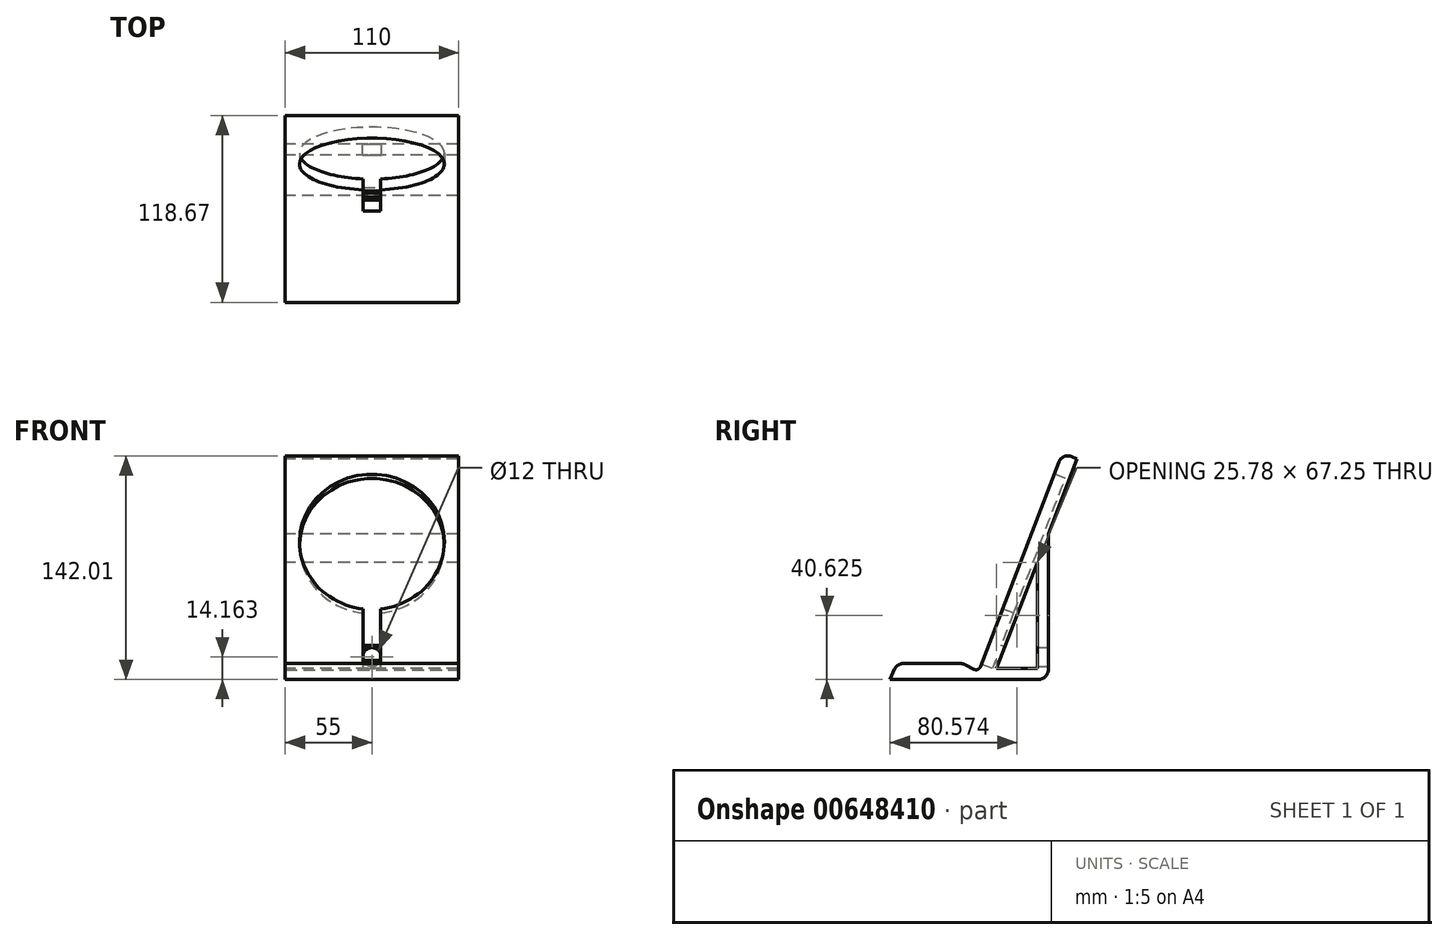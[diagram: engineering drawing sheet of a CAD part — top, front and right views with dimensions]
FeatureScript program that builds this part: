
annotation { "Feature Type Name" : "Feature", "Feature Type Description" : "" }
export const myFeature = defineFeature(function(context is Context, id is Id, definition is map)
    precondition{}
    {
        {
            var Q0;
            Q0=qCreatedBy(makeId("Right.planeOp"),FACE);
            var sketch = newSketch(context, id + "F0", { "sketchPlane" : qUnion([Q0])});
            skLineSegment(sketch, "E0", {"start": v(-0.23, -35.33) * mm, "end": v(53.11, 103.83) * mm});
            skLineSegment(sketch, "E1.0", {"start": v(8.6, -40.22) * mm, "end": v(62.27, 99.78) * mm});
            skLineSegment(sketch, "E1.1", {"start": v(-56.4, -40.11) * mm, "end": v(8.6, -40.22) * mm});
            skLineSegment(sketch, "E2", {"start": v(-51.97, -30.12) * mm, "end": v(-56.4, -40.11) * mm});
            skLineSegment(sketch, "E3", {"start": v(62.27, 99.78) * mm, "end": v(53.11, 103.83) * mm});
            skLineSegment(sketch, "E4", {"start": v(-9.93, -30.2) * mm, "end": v(-0.23, -35.33) * mm});
            skPoint(sketch, "E5.orphan", {"position": v(0, -34.72) * mm});
            skLineSegment(sketch, "E6", {"start": v(-9.93, -30.2) * mm, "end": v(-51.97, -30.12) * mm});
            skLineSegment(sketch, "E7", {"start": v(37.06, 34.03) * mm, "end": v(37.06, -33.22) * mm});
            skLineSegment(sketch, "E8", {"start": v(44.06, -40.22) * mm, "end": v(8.6, -40.22) * mm});
            skLineSegment(sketch, "E9.0", {"start": v(44.06, 52.3) * mm, "end": v(44.06, -40.22) * mm});
            skLineSegment(sketch, "E10.0", {"start": v(37.06, -33.22) * mm, "end": v(11.28, -33.22) * mm});
            skPoint(sketch, "E11.orphan", {"position": v(37.06, -40.22) * mm});
            skSolve(sketch);
        }
        {
            var Q0;
            {var subQ0=sQuery(id+"F0.wireOp",EDGE,"E7");Q0=makeQuery(id+"F0.imprint","IMPRINT",FACE,{"disambiguationData":[TD([[makeQuery(id+"F0.imprint","IMPRINT",EDGE,{"derivedFrom":subQ0}),1.0]])]});}
            var Q1;
            Q1=makeQuery(id+"F0.imprint","IMPRINT",FACE,{"disambiguationData":[TD([[makeQuery(id+"F0.imprint","IMPRINT",EDGE,{"derivedFrom":sQuery(id+"F0.wireOp",EDGE,"E0")}),-1.0]])]});
            extrude(context, id + "F1", {"entities" : qUnion([Q0, Q1]), "endBound" : BoundingType.SYMMETRIC, "depth" : 110 * mm, "offsetDistance" : 25 * mm});
        }
        {
            var Q0;
            Q0=makeQuery(id+"F1.opExtrude","SWEPT_EDGE",EDGE,{"disambiguationData":[OSD([sQuery(id+"F0.wireOp",EDGE,"E4"),sQuery(id+"F0.wireOp",EDGE,"E6")])]});
            var Q1;
            Q1=makeQuery(id+"F1.opExtrude","SWEPT_EDGE",EDGE,{"disambiguationData":[OSD([sQuery(id+"F0.wireOp",EDGE,"E2"),sQuery(id+"F0.wireOp",EDGE,"E6")])]});
            var Q2;
            Q2=makeQuery(id+"F1.opExtrude","SWEPT_EDGE",EDGE,{"disambiguationData":[OSD([sQuery(id+"F0.wireOp",EDGE,"E8"),sQuery(id+"F0.wireOp",EDGE,"E9.0")])]});
            var Q3;
            Q3=makeQuery(id+"F1.opExtrude","SWEPT_EDGE",EDGE,{"disambiguationData":[OSD([sQuery(id+"F0.wireOp",EDGE,"E0"),sQuery(id+"F0.wireOp",EDGE,"E3")])]});
            fillet(context, id + "F2", {"entities" : qUnion([Q0, Q1, Q2, Q3]), "radius" : 6 * mm, "tangentPropagation" : true, "allowEdgeOverflow" : false});
        }
        {
            var Q0;
            Q0=makeQuery(id+"F1.opExtrude","SWEPT_EDGE",EDGE,{"disambiguationData":[OSD([sQuery(id+"F0.wireOp",EDGE,"E0"),sQuery(id+"F0.wireOp",EDGE,"E4")])]});
            fillet(context, id + "F3", {"entities" : qUnion([Q0]), "radius" : 3 * mm, "tangentPropagation" : true, "allowEdgeOverflow" : false});
        }
        {
            var Q0;
            Q0=makeQuery(id+"F1.opExtrude","SWEPT_FACE",FACE,{"disambiguationData":[OSD([sQuery(id+"F0.wireOp",EDGE,"E0")])]});
            var sketch = newSketch(context, id + "F4", { "sketchPlane" : qUnion([Q0])});
            skPoint(sketch, "E12", {"position": v(0, 55.31) * mm});
            skArc(sketch, "E13", {"start": v(5.5, 10.55) * mm, "mid": v(0, 100.41) * mm, "end": v(-5.5, 10.55) * mm});
            skArc(sketch, "E14", {"start": v(5.5, 9.64) * mm, "mid": v(0, 101.31) * mm, "end": v(-5.5, 9.64) * mm});
            skPoint(sketch, "E15.middle", {"position": v(-5.97, 9.58) * mm});
            skLineSegment(sketch, "E16.bottom", {"start": v(-5.5, 10.6) * mm, "end": v(5.5, 10.6) * mm});
            skLineSegment(sketch, "E16.top", {"start": v(-5.5, -28.02) * mm, "end": v(5.5, -28.02) * mm});
            skLineSegment(sketch, "E16.left", {"start": v(-5.5, 10.6) * mm, "end": v(-5.5, 10.55) * mm});
            skLineSegment(sketch, "E16.right", {"start": v(5.5, 10.6) * mm, "end": v(5.5, 10.55) * mm});
            skPoint(sketch, "E16.middle", {"position": v(0, -8.71) * mm});
            skLineSegment(sketch, "E17.trimOffspring", {"start": v(5.5, 9.64) * mm, "end": v(5.5, -28.02) * mm});
            skLineSegment(sketch, "E18.trimOffspring", {"start": v(-5.5, 9.64) * mm, "end": v(-5.5, -28.02) * mm});
            skSolve(sketch);
        }
        {
            var Q0;
            {var subQ5=sQuery(id+"F4.wireOp",EDGE,"E16.bottom");Q0=makeQuery(id+"F4.imprint","IMPRINT",FACE,{"disambiguationData":[TD([[makeQuery(id+"F4.imprint","IMPRINT",EDGE,{"derivedFrom":subQ5}),1.0]])]});}
            var Q1;
            {var subQ5=sQuery(id+"F4.wireOp",EDGE,"E16.top");Q1=makeQuery(id+"F4.imprint","IMPRINT",FACE,{"disambiguationData":[TD([[makeQuery(id+"F4.imprint","IMPRINT",EDGE,{"derivedFrom":subQ5}),1.0]])]});}
            var Q2;
            {var subQ0=sQuery(id+"F4.wireOp",EDGE,"E16.left");var subQ1=sQuery(id+"F4.wireOp",EDGE,"E13");var subQ2=makeQuery(id+"F4.imprint","INTERSECT",VERTEX,{"derivedFrom":[subQ1,subQ0]});Q2=makeQuery(id+"F4.imprint","IMPRINT",FACE,{"disambiguationData":[TD([[makeQuery(id+"F4.imprint","IMPRINT",EDGE,{"disambiguationData":[TD([[subQ2,-1.0]])],"derivedFrom":subQ1}),-1.0]])]});}
            extrude(context, id + "F5", {"entities" : qUnion([Q0, Q1, Q2]), "operationType" : NewBodyOperationType.REMOVE, "oppositeDirection" : true, "depth" : 7.5 * mm, "offsetDistance" : 25 * mm});
        }
        {
            var Q0;
            Q0=makeQuery(id+"F5.boolean.opBoolean","COPY",FACE,{"derivedFrom":makeQuery(id+"F5.opExtrude","CAP_FACE",FACE,{"disambiguationData":[OSD([sQuery(id+"F4.wireOp",EDGE,"E14"),sQuery(id+"F4.wireOp",EDGE,"E16.top"),sQuery(id+"F4.wireOp",EDGE,"E17.trimOffspring"),sQuery(id+"F4.wireOp",EDGE,"E18.trimOffspring")])],"isStart":false})});
            var sketch = newSketch(context, id + "F6", { "sketchPlane" : qUnion([Q0])});
            skLineSegment(sketch, "E19.bottom", {"start": v(-5.5, -22.47) * mm, "end": v(5.5, -22.47) * mm});
            skLineSegment(sketch, "E19.top", {"start": v(-5.5, -12.47) * mm, "end": v(5.5, -12.47) * mm});
            skLineSegment(sketch, "E19.left", {"start": v(-5.5, -22.47) * mm, "end": v(-5.5, -12.47) * mm});
            skLineSegment(sketch, "E19.right", {"start": v(5.5, -22.47) * mm, "end": v(5.5, -12.47) * mm});
            skPoint(sketch, "E19.middle", {"position": v(0, -17.47) * mm});
            skSolve(sketch);
        }
        {
            var Q0;
            Q0 = qSketchRegion(id + "F6", true);
            extrude(context, id + "F7", {"entities" : qUnion([Q0]), "operationType" : NewBodyOperationType.REMOVE, "oppositeDirection" : true, "depth" : 12 * mm, "offsetDistance" : 25 * mm});
        }
        {
            var Q0;
            Q0=makeQuery(id+"F1.opExtrude","SWEPT_FACE",FACE,{"disambiguationData":[OSD([sQuery(id+"F0.wireOp",EDGE,"E9.0")])]});
            var sketch = newSketch(context, id + "F8", { "sketchPlane" : qUnion([Q0])});
            skCircle(sketch, "E20", {"center": v(0, -26.06) * mm, "radius": 6 * mm});
            skSolve(sketch);
        }
        {
            var Q0;
            Q0=sQuery(id+"F8.wireOp",VERTEX,"E20.center");
            var Q1;
            Q1=makeQuery(id+"F1.opExtrude","SWEPT_BODY",BODY,{"disambiguationData":[OSD([sQuery(id+"F0.wireOp",EDGE,"E0"),sQuery(id+"F0.wireOp",EDGE,"E1.0"),sQuery(id+"F0.wireOp",EDGE,"E1.1"),sQuery(id+"F0.wireOp",EDGE,"E2"),sQuery(id+"F0.wireOp",EDGE,"E3"),sQuery(id+"F0.wireOp",EDGE,"E4"),sQuery(id+"F0.wireOp",EDGE,"E6"),sQuery(id+"F0.wireOp",EDGE,"E7"),sQuery(id+"F0.wireOp",EDGE,"E8"),sQuery(id+"F0.wireOp",EDGE,"E9.0"),sQuery(id+"F0.wireOp",EDGE,"E10.0")])]});
            hole(context, id + "F9", {"style" : HoleStyle.SIMPLE, "endStyle" : HoleEndStyle.BLIND, "holeDiameter" : 12 * mm, "majorDiameter" : 5 * mm, "holeDepth" : 13 * mm, "isTappedThrough" : true, "tappedDepth" : 12 * mm, "tapClearance" : 3, "locations" : qUnion([Q0]), "scope" : qUnion([Q1])});
        }
    });
